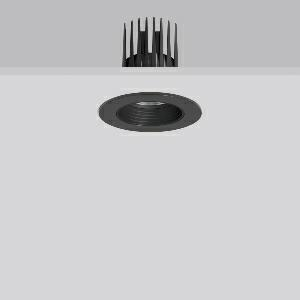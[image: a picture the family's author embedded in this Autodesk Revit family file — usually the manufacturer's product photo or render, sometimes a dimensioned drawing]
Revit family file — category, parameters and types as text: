
# Revit family: heledon_mini_e_901751_003_76_61a5
name_source: partatom
category: Lighting Fixtures
units: mm (PartAtom-declared; Revit-internal decimal feet)

## family parameters
Cut with Voids When Loaded = No
Host = Face
Light Source = No
Part Type = Normal
Room Calculation Point = No
Round Connector Dimension = Use Diameter
Shared = No

## types (1)
- HELEDON mini E (1 x LED Modul 930, 3150 lm, 3000)
    Apparent Load = 29 VA
    Approval mark = CE
    CIE Flux Codes = 99 100 100 100 100
    Color Rendering = 90
    Color Temperature = 3000
    Default Elevation = 1800 mm
    Description = Series: HELEDON mini
Round recessed downlight. Housing: die-cast aluminium, powder-coated. Black plastic ring and recessed LED to prevent glare from the side. Optical assembly with lens made of plastic (polycarbonate) for the best homogeneous light distribution - can be changed without tools. Best colour rendering index Ra>90. Suitable for Recessed ceiling mounting. Installation without tools thanks to spring fastening system. Including separate LED converter with connecting cable 600 mm.High quality converter without flickering and stroboscopic effect. Through-wiring box (5 pole) available as accessory. The following accessories can be mounted without use of tools: interchangeable lenses, decorative glasses, honeycomb louvre, clear and frosted diffusers, white interchangeable plastic ring. 
Colour: deep black, matt (RAL 9005)
Diameter: 124 mm
Height: 3 mm
Cut-out diameter: 114 mm
Recess height: 170 mm
Luminaire: recess height: 120 mm
Lamp: LED
Socket: without socket
Colour temperature: 3000K
Colour rendering index (CRI): 92
System power: 29 W
Rated luminous flux: 3150 lm
Luminous efficiency: 109 lm/W
Control gear: Converter, dimmable, DALI
Protection class: II
Type of protection: IP 20
    Height = 0 mm  [stored 0 ft]
    Lamp = 1 x LED Modul 930
    Lamp Light Flux = 3150 lm
    Lamp count = 1
    Length = 124 mm  [stored 0.406824 ft]
    Lifetime = 50000 h
    Luminous efficacy = 109 lm/W
    Manufacturer = RZB
    ModVariant = No
    Model = 901751.003.76
    Mounting Place = Ceiling
    Mounting Type = Recessed
    Number of Poles = 1
    OnlyDefault = Yes
    Power Factor = 1
    Product Name = HELEDON mini E
    Product group = Recessed downlights
    ProductGroupID = 402
    Protection Class = Protection class II
    Protection Degree = IP 20
    RLX_Detail_Level = 1
    RLX_Emergency_Light_Flux = 0 lm
    RLX_Emergency_Type = 0
    RLX_Emergency_Type_DB = No
    RlxData = <blob elided: 126597 chars, md5=f51899c6>
    Socket = socket
    Standby Power = 0 W
    System Light Flux = 3150 lm
    System Power = 29 W
    Type Comments = Product without accessories
    Type Image = 901656.003.jpg
    URL = http://relux.com
    VarID = ---
    Voltage = 230 V
    Voltage Range = 220-240 V
    Weight = 0.00 kg
    Width = 0 mm  [stored 0 ft]

note: [stored X ft] marks values corroborated as IEEE doubles in the binary element streams (Revit-internal decimal feet)

## geometry (parser evidence)
native form markers: Blend x4, Sweep x10
no freeform markers — native parametric forms only
